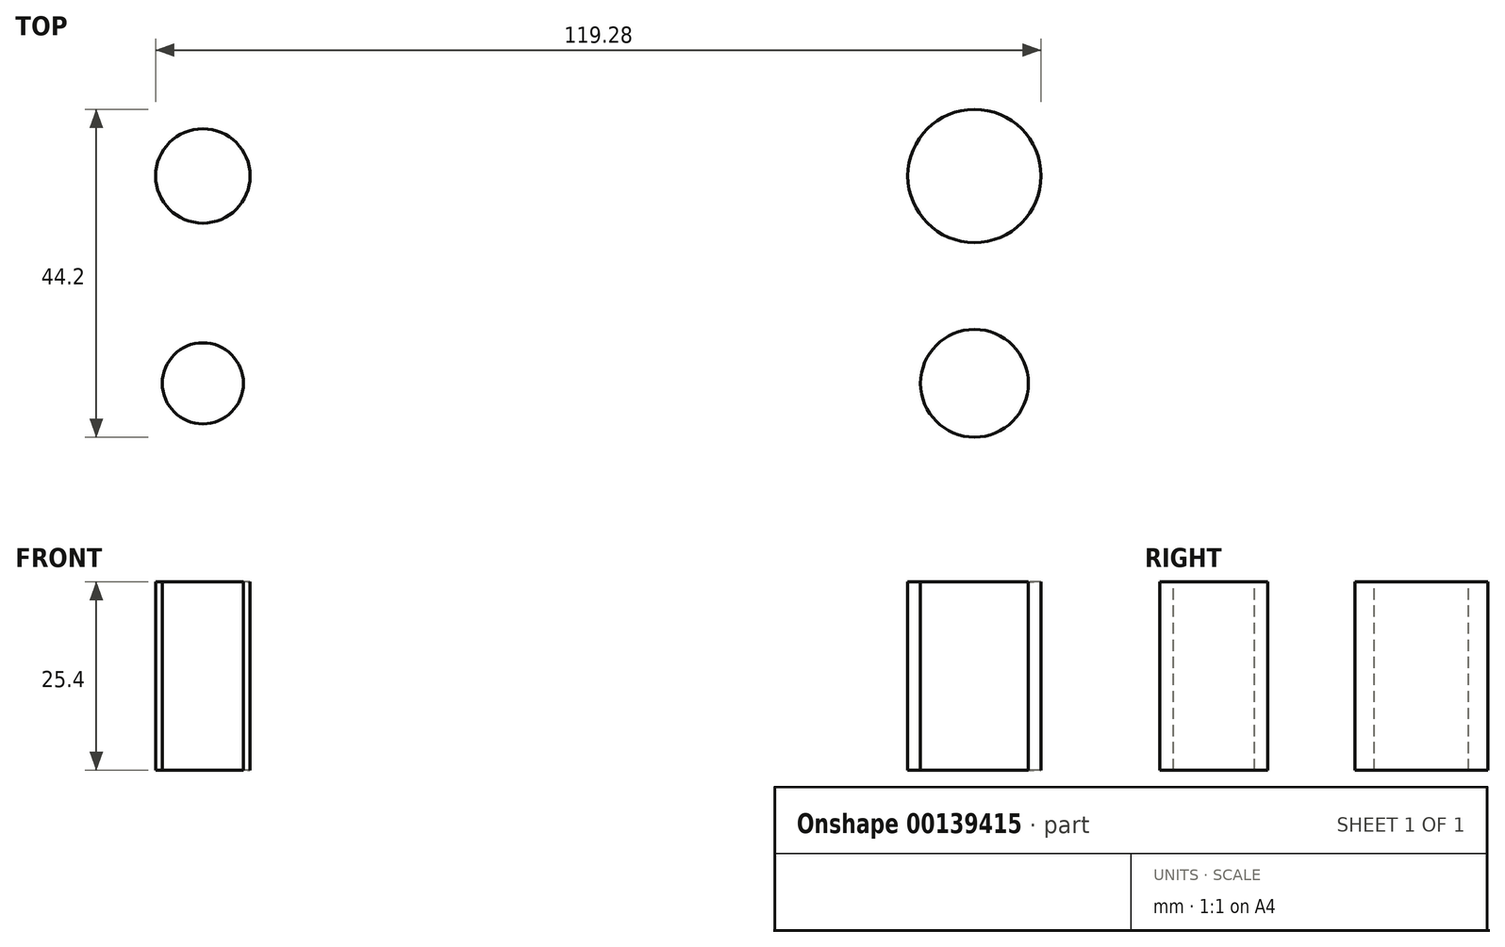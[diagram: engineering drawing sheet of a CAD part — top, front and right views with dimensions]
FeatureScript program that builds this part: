
annotation { "Feature Type Name" : "Feature", "Feature Type Description" : "" }
export const myFeature = defineFeature(function(context is Context, id is Id, definition is map)
    precondition{}
    {
        {
            var Q0;
            Q0=qCreatedBy(makeId("Top.planeOp"),FACE);
            var sketch = newSketch(context, id + "F0", { "sketchPlane" : qUnion([Q0])});
            skLineSegment(sketch, "E0.bottom", {"start": v(-48.86, 18.44) * mm, "end": v(55.08, 18.44) * mm});
            skLineSegment(sketch, "E0.top", {"start": v(-48.86, -9.51) * mm, "end": v(55.08, -9.51) * mm});
            skLineSegment(sketch, "E0.left", {"start": v(-48.86, 18.44) * mm, "end": v(-48.86, -9.51) * mm});
            skLineSegment(sketch, "E0.right", {"start": v(55.08, 18.44) * mm, "end": v(55.08, -9.51) * mm});
            skCircle(sketch, "E1", {"center": v(-48.86, -9.51) * mm, "radius": 5.46 * mm});
            skCircle(sketch, "E2", {"center": v(-48.86, 18.44) * mm, "radius": 6.36 * mm});
            skCircle(sketch, "E3", {"center": v(55.08, 18.44) * mm, "radius": 8.98 * mm});
            skCircle(sketch, "E4", {"center": v(55.08, -9.51) * mm, "radius": 7.27 * mm});
            skSolve(sketch);
        }
        {
            var Q0;
            Q0=sQuery(id+"F0.wireOp",EDGE,"E2");
            var Q1;
            Q1=sQuery(id+"F0.wireOp",EDGE,"E1");
            var Q2;
            Q2=sQuery(id+"F0.wireOp",EDGE,"E4");
            var Q3;
            Q3=sQuery(id+"F0.wireOp",EDGE,"E3");
            extrude(context, id + "F1", {"bodyType" : ToolBodyType.SURFACE, "surfaceEntities" : qUnion([Q0, Q1, Q2, Q3]), "depth" : 25.4 * mm});
        }
    });
